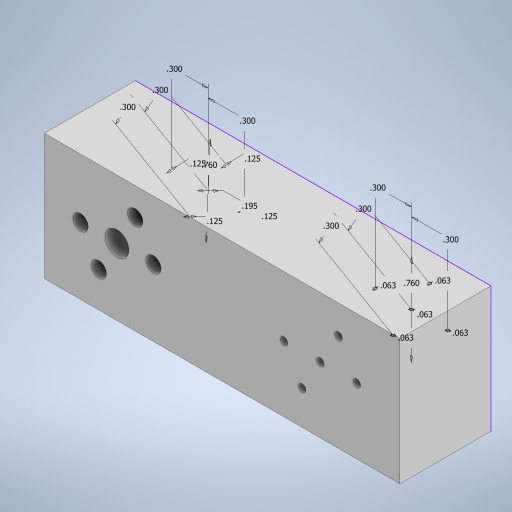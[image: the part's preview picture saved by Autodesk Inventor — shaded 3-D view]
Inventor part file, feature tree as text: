
AUTODESK INVENTOR PART (.ipt)
format: ipt  version: 2023 (Build 270158000, 158)  size: 276,992 bytes
history: native  units: in
note: dims shown in document units (in); Inventor stores cm internally (conversion verified against a paired STEP export)
features: extrude x2, sketch x1
ambient origin geometry x8: Origin, YZ Plane, XZ Plane, XY Plane, X Axis, Y Axis, Z Axis, Center Point
bodies: Body1 (feature_tree)
feature tree (3):
  sketch  "Sketch1"  dims[d3=0.866in d15=0.75in d37=0.75in d69=0.0625in d70=0.0625in d73=0.75in d74=0.0in d75=0.0625in d76=0.0625in d79=0.3in d80=0.3in d82=0.0625in d83=0.3in d84=0.3in d85=0.125in d86=0.125in d87=0.125in d88=0.125in d89=0.3in d90=0.3in d91=0.195in d92=0.3in d93=0.3in d95=0.76in d96=0.76in d97=0.47in d98=0.0in]
  extrude  "Extrusion14"  Depth=0.75in
  extrude  "Extrusion15"  Depth=0.0625in
